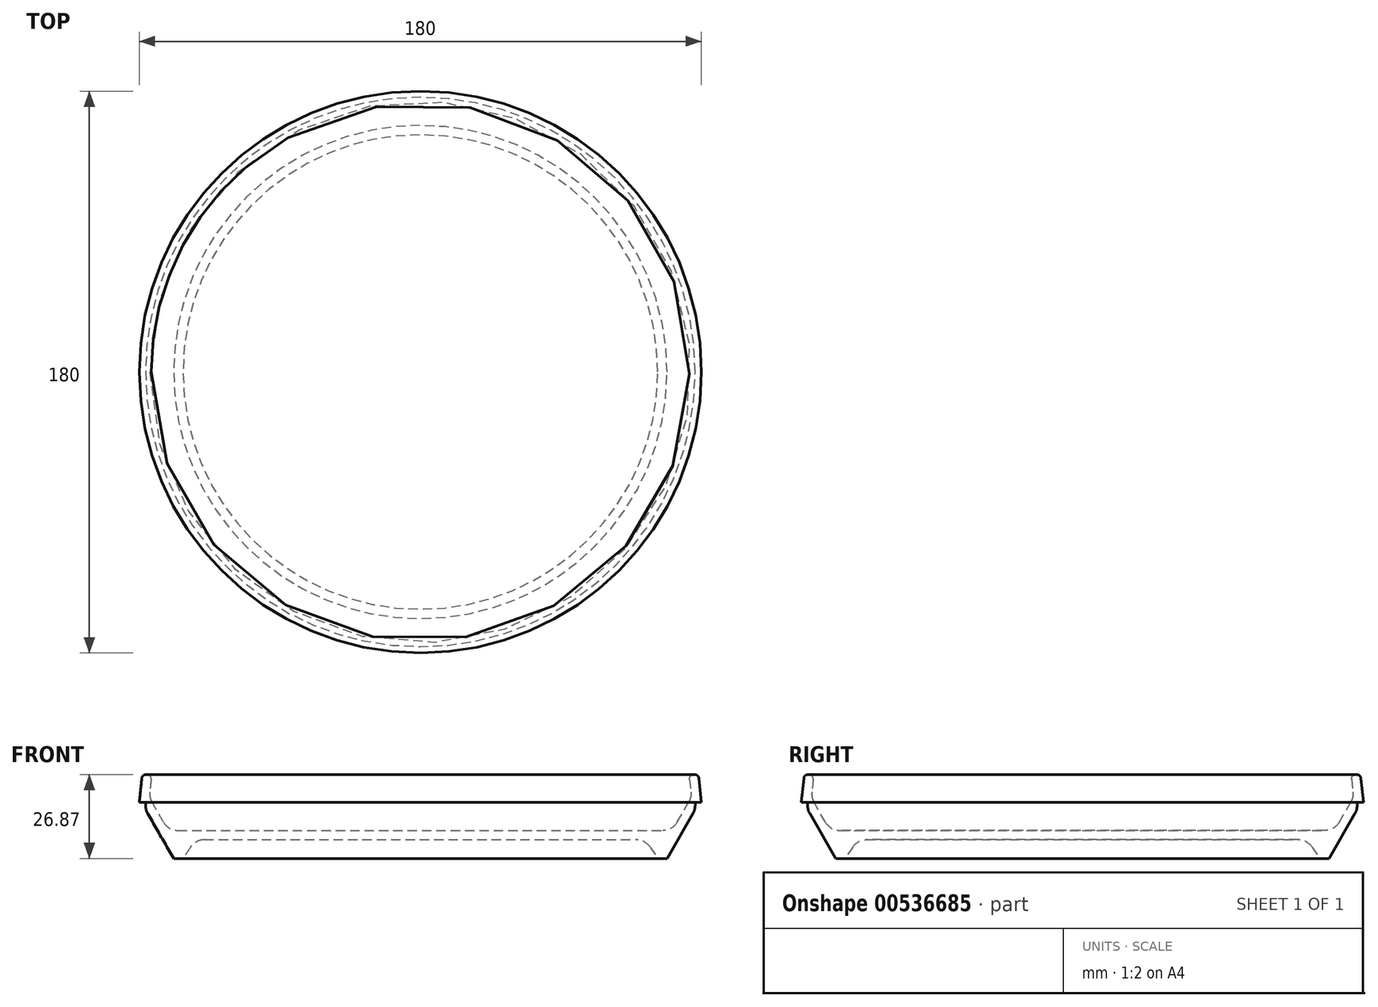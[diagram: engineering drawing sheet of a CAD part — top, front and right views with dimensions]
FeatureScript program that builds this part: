
annotation { "Feature Type Name" : "Feature", "Feature Type Description" : "" }
export const myFeature = defineFeature(function(context is Context, id is Id, definition is map)
    precondition{}
    {
        {
            var Q0;
            Q0=qCreatedBy(makeId("Front.planeOp"),FACE);
            var sketch = newSketch(context, id + "F0", { "sketchPlane" : qUnion([Q0])});
            skLineSegment(sketch, "E0", {"start": v(0, 6) * mm, "end": v(69.18, 6) * mm});
            skLineSegment(sketch, "E1", {"start": v(73.56, 3.65) * mm, "end": v(76, 0) * mm});
            skLineSegment(sketch, "E2", {"start": v(76, 0) * mm, "end": v(79, 0) * mm});
            skLineSegment(sketch, "E3", {"start": v(79, 0) * mm, "end": v(87.3, 14.37) * mm});
            skLineSegment(sketch, "E4", {"start": v(88, 17) * mm, "end": v(88, 18) * mm});
            skLineSegment(sketch, "E5", {"start": v(88, 18) * mm, "end": v(90, 18) * mm});
            skLineSegment(sketch, "E6", {"start": v(90, 18) * mm, "end": v(89.19, 25.7) * mm});
            skLineSegment(sketch, "E7", {"start": v(87.76, 26.86) * mm, "end": v(87.36, 26.82) * mm});
            skLineSegment(sketch, "E8", {"start": v(86.2, 25.4) * mm, "end": v(86.64, 21.25) * mm});
            skLineSegment(sketch, "E9", {"start": v(85.97, 18.06) * mm, "end": v(82.25, 11.63) * mm});
            skLineSegment(sketch, "E10", {"start": v(77.7, 9) * mm, "end": v(0, 9) * mm});
            skLineSegment(sketch, "E11", {"start": v(0, 9) * mm, "end": v(0, 6) * mm});
            skPoint(sketch, "E12.visualSharp", {"position": v(72, 6) * mm});
            skArc(sketch, "E12.filletArc", {"start": v(73.56, 3.65) * mm, "mid": v(71.67, 5.38) * mm, "end": v(69.18, 6) * mm});
            skPoint(sketch, "E13.visualSharp", {"position": v(80.73, 9) * mm});
            skArc(sketch, "E13.filletArc", {"start": v(77.7, 9) * mm, "mid": v(80.32, 9.7) * mm, "end": v(82.25, 11.63) * mm});
            skPoint(sketch, "E14.visualSharp", {"position": v(86.82, 19.55) * mm});
            skArc(sketch, "E14.filletArc", {"start": v(85.97, 18.06) * mm, "mid": v(86.56, 19.6) * mm, "end": v(86.64, 21.25) * mm});
            skPoint(sketch, "E15.visualSharp", {"position": v(88, 15.59) * mm});
            skArc(sketch, "E15.filletArc", {"start": v(87.3, 14.37) * mm, "mid": v(87.82, 15.64) * mm, "end": v(88, 17) * mm});
            skPoint(sketch, "E16.visualSharp", {"position": v(89.05, 27) * mm});
            skArc(sketch, "E16.filletArc", {"start": v(89.19, 25.7) * mm, "mid": v(88.72, 26.58) * mm, "end": v(87.76, 26.86) * mm});
            skPoint(sketch, "E17.visualSharp", {"position": v(86.07, 26.69) * mm});
            skArc(sketch, "E17.filletArc", {"start": v(87.36, 26.82) * mm, "mid": v(86.49, 26.35) * mm, "end": v(86.2, 25.4) * mm});
            skLineSegment(sketch, "E18", {"start": v(90, 18) * mm, "end": v(90, 27) * mm, "construction": true});
            skLineSegment(sketch, "E19", {"start": v(0, 0) * mm, "end": v(0, 25.7) * mm, "construction": true});
            skSolve(sketch);
        }
        {
            var Q0;
            Q0=qSketchRegion(id+"F0",true);
            var Q1;
            Q1=sQuery(id+"F0.wireOp",EDGE,"E19");
            revolve(context, id + "F1", {"entities" : qUnion([Q0]), "axis" : qUnion([Q1]), "revolveType" : RevolveType.FULL});
        }
    });
